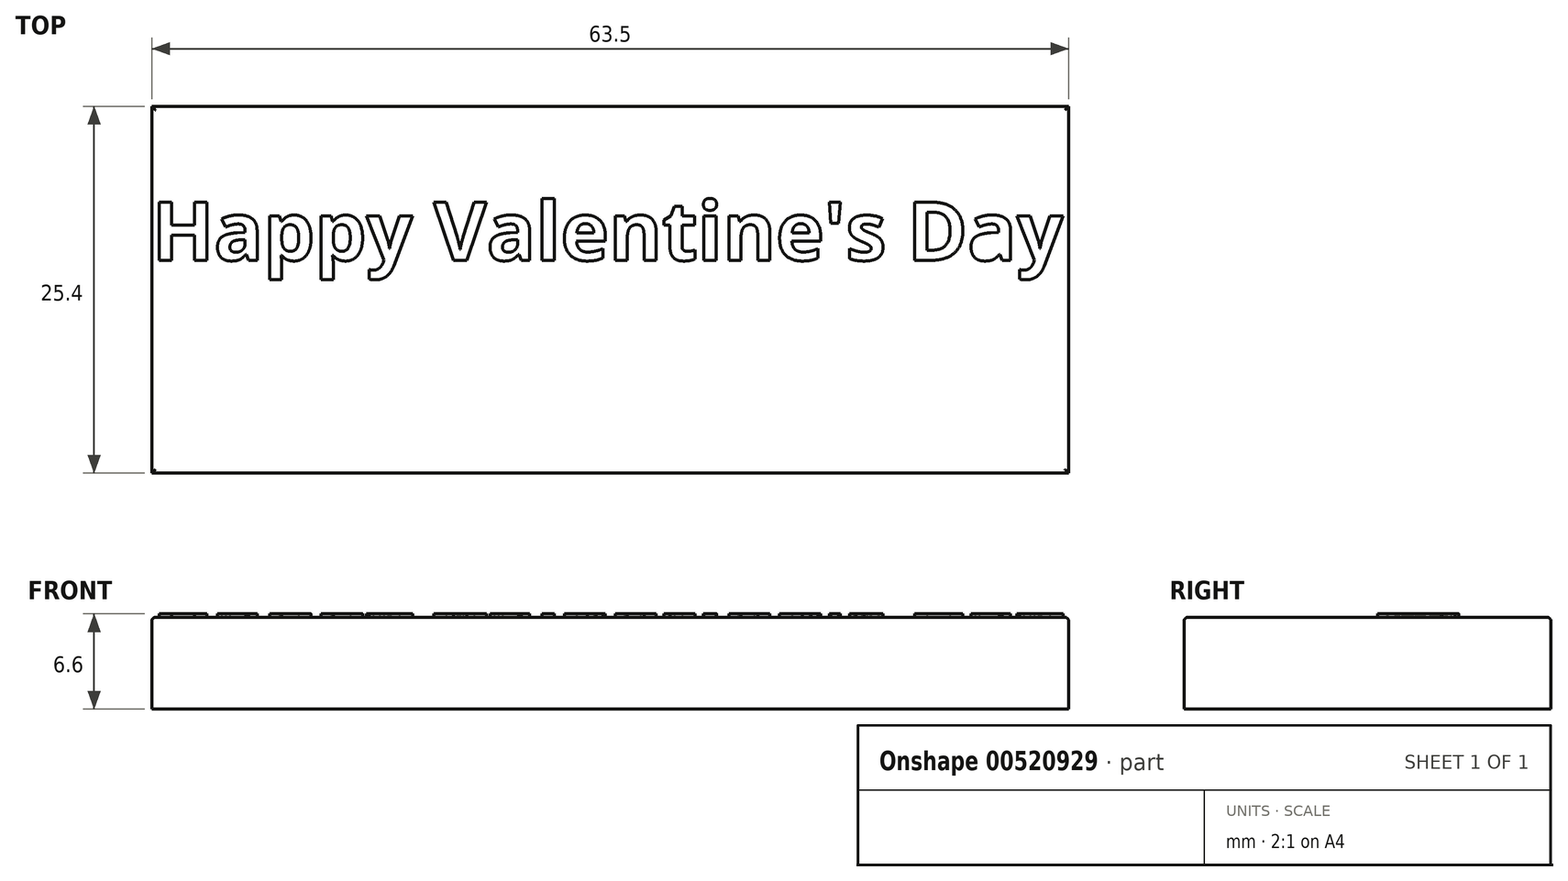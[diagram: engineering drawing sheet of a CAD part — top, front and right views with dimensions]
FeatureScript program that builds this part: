
annotation { "Feature Type Name" : "Feature", "Feature Type Description" : "" }
export const myFeature = defineFeature(function(context is Context, id is Id, definition is map)
    precondition{}
    {
        {
            var Q0;
            Q0=qCreatedBy(makeId("Top.planeOp"),FACE);
            var sketch = newSketch(context, id + "F0", { "sketchPlane" : qUnion([Q0])});
            skLineSegment(sketch, "E0.bottom", {"start": v(-51, 0) * mm, "end": v(12.5, 0) * mm});
            skLineSegment(sketch, "E0.top", {"start": v(-51, -25.4) * mm, "end": v(12.5, -25.4) * mm});
            skLineSegment(sketch, "E0.left", {"start": v(-51, 0) * mm, "end": v(-51, -25.4) * mm});
            skLineSegment(sketch, "E0.right", {"start": v(12.5, 0) * mm, "end": v(12.5, -25.4) * mm});
            skSolve(sketch);
        }
        {
            var Q0;
            Q0=makeQuery(id+"F0.imprint","IMPRINT",FACE,{"disambiguationData":[TD([[makeQuery(id+"F0.imprint","IMPRINT",EDGE,{"derivedFrom":sQuery(id+"F0.wireOp",EDGE,"E0.bottom")}),-1.0]])]});
            extrude(context, id + "F1", {"entities" : qUnion([Q0]), "depth" : 6.35 * mm, "offsetDistance" : 25.4 * mm});
        }
        {
            var Q0;
            Q0=makeQuery(id+"F1.opExtrude","CAP_FACE",FACE,{"disambiguationData":[OSD([sQuery(id+"F0.wireOp",EDGE,"E0.bottom"),sQuery(id+"F0.wireOp",EDGE,"E0.top"),sQuery(id+"F0.wireOp",EDGE,"E0.left"),sQuery(id+"F0.wireOp",EDGE,"E0.right")])],"isStart":false});
            var sketch = newSketch(context, id + "F2", { "sketchPlane" : qUnion([Q0])});
            skText(sketch, "E1", { "text": "Happy Valentine\'s Day", "fontName": "OpenSans-Bold.ttf"});
            const initialGuessF2  = {"E1": [-0.051, -0.01066, 1, 0, 0.00406]};
            skSetInitialGuess(sketch, initialGuessF2);
            skSolve(sketch);
        }
        {
            var Q0;
            Q0=makeQuery(id+"F2.imprint","IMPRINT",FACE,{"disambiguationData":[TD([[makeQuery(id+"F2.imprint","IMPRINT",EDGE,{"derivedFrom":sQuery(id+"F2.wireOp",EDGE,"E1.sketch_text.stroke-300")}),1.0]])]});
            var Q1;
            Q1 = qSketchRegion(id + "F2", true);
            extrude(context, id + "F3", {"entities" : qUnion([Q0, Q1]), "operationType" : NewBodyOperationType.ADD, "depth" : 0.25 * mm, "offsetDistance" : 25.4 * mm});
        }
        {
            var Q0;
            Q0=makeQuery(id+"F1.opExtrude","CAP_EDGE",EDGE,{"disambiguationData":[OSD([sQuery(id+"F0.wireOp",EDGE,"E0.left")])],"isStart":false});
            var Q1;
            Q1=makeQuery(id+"F1.opExtrude","CAP_EDGE",EDGE,{"disambiguationData":[OSD([sQuery(id+"F0.wireOp",EDGE,"E0.bottom")])],"isStart":false});
            var Q2;
            Q2=makeQuery(id+"F1.opExtrude","CAP_EDGE",EDGE,{"disambiguationData":[OSD([sQuery(id+"F0.wireOp",EDGE,"E0.top")])],"isStart":false});
            var Q3;
            Q3=makeQuery(id+"F1.opExtrude","CAP_EDGE",EDGE,{"disambiguationData":[OSD([sQuery(id+"F0.wireOp",EDGE,"E0.right")])],"isStart":false});
            fillet(context, id + "F4", {"entities" : qUnion([Q0, Q1, Q2, Q3]), "radius" : 0.25 * mm, "tangentPropagation" : true, "allowEdgeOverflow" : false});
        }
    });
